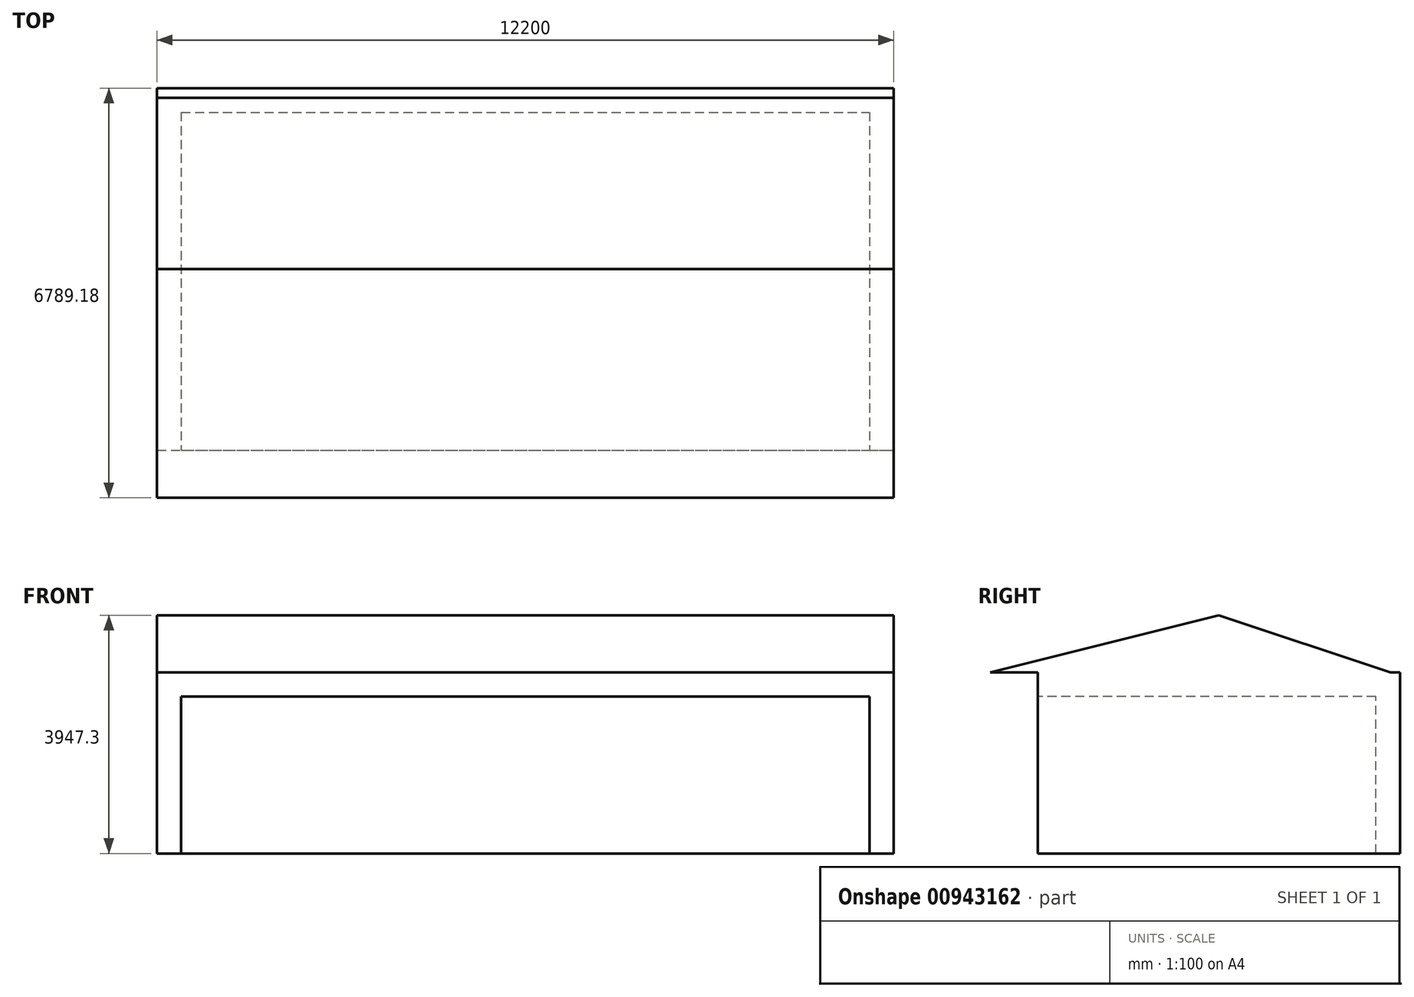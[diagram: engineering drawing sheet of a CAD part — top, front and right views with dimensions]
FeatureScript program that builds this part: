
annotation { "Feature Type Name" : "Feature", "Feature Type Description" : "" }
export const myFeature = defineFeature(function(context is Context, id is Id, definition is map)
    precondition{}
    {
        {
            var Q0;
            Q0=qCreatedBy(makeId("Top.planeOp"),FACE);
            var sketch = newSketch(context, id + "F0", { "sketchPlane" : qUnion([Q0])});
            skLineSegment(sketch, "E0.bottom", {"start": v(0, 0) * mm, "end": v(12200, 0) * mm});
            skLineSegment(sketch, "E0.top", {"start": v(0, -6000) * mm, "end": v(12200, -6000) * mm});
            skLineSegment(sketch, "E0.left", {"start": v(0, 0) * mm, "end": v(0, -6000) * mm});
            skLineSegment(sketch, "E0.right", {"start": v(12200, 0) * mm, "end": v(12200, -6000) * mm});
            skSolve(sketch);
        }
        {
            var Q0;
            Q0 = qSketchRegion(id + "F0", true);
            extrude(context, id + "F1", {"entities" : qUnion([Q0]), "depth" : 3000 * mm, "offsetDistance" : 25 * mm});
        }
        {
            var Q0;
            Q0=makeQuery(id+"F1.opExtrude","SWEPT_FACE",FACE,{"disambiguationData":[OSD([sQuery(id+"F0.wireOp",EDGE,"E0.left")])]});
            var sketch = newSketch(context, id + "F2", { "sketchPlane" : qUnion([Q0])});
            skLineSegment(sketch, "E1", {"start": v(0, 3000) * mm, "end": v(7000, 3000) * mm});
            skLineSegment(sketch, "E2", {"start": v(7000, 3000) * mm, "end": v(3000, 4000) * mm});
            skLineSegment(sketch, "E3", {"start": v(3000, 4000) * mm, "end": v(0, 3000) * mm});
            skSolve(sketch);
        }
        {
            var Q0;
            Q0 = qSketchRegion(id + "F2", true);
            extrude(context, id + "F3", {"entities" : qUnion([Q0]), "operationType" : NewBodyOperationType.ADD, "oppositeDirection" : true, "depth" : 12200 * mm, "offsetDistance" : 25 * mm});
        }
        {
            var Q0;
            Q0=makeQuery(id+"F1.opExtrude","SWEPT_FACE",FACE,{"disambiguationData":[OSD([sQuery(id+"F0.wireOp",EDGE,"E0.top")])]});
            var sketch = newSketch(context, id + "F4", { "sketchPlane" : qUnion([Q0])});
            skLineSegment(sketch, "E4.bottom", {"start": v(400, 0) * mm, "end": v(11800, 0) * mm});
            skLineSegment(sketch, "E4.top", {"start": v(400, 2600) * mm, "end": v(11800, 2600) * mm});
            skLineSegment(sketch, "E4.left", {"start": v(400, 0) * mm, "end": v(400, 2600) * mm});
            skLineSegment(sketch, "E4.right", {"start": v(11800, 0) * mm, "end": v(11800, 2600) * mm});
            skSolve(sketch);
        }
        {
            var Q0;
            Q0 = qSketchRegion(id + "F4", true);
            extrude(context, id + "F5", {"entities" : qUnion([Q0]), "operationType" : NewBodyOperationType.REMOVE, "oppositeDirection" : true, "depth" : 5600 * mm, "offsetDistance" : 25 * mm});
        }
        {
            var Q0;
            Q0=makeQuery(id+"F3.boolean.opBoolean","MERGE",FACE,{"derivedFrom":[makeQuery(id+"F1.opExtrude","SWEPT_FACE",FACE,{"disambiguationData":[OSD([sQuery(id+"F0.wireOp",EDGE,"E0.left")])]}),makeQuery(id+"F3.opExtrude","CAP_FACE",FACE,{"disambiguationData":[OSD([sQuery(id+"F2.wireOp",EDGE,"E1"),sQuery(id+"F2.wireOp",EDGE,"E2"),sQuery(id+"F2.wireOp",EDGE,"E3")])],"isStart":true})]});
            var sketch = newSketch(context, id + "F6", { "sketchPlane" : qUnion([Q0])});
            skLineSegment(sketch, "E5", {"start": v(0, 3000) * mm, "end": v(3000, 4000) * mm});
            skLineSegment(sketch, "E6", {"start": v(3000, 4000) * mm, "end": v(7000, 3000) * mm});
            skLineSegment(sketch, "E7", {"start": v(7000, 3000) * mm, "end": v(6789.18, 3000) * mm});
            skLineSegment(sketch, "E8", {"start": v(6789.18, 3000) * mm, "end": v(3000, 3947.3) * mm});
            skLineSegment(sketch, "E9", {"start": v(3000, 3947.3) * mm, "end": v(158.11, 3000) * mm});
            skLineSegment(sketch, "E10", {"start": v(158.11, 3000) * mm, "end": v(0, 3000) * mm});
            skSolve(sketch);
        }
        {
            var Q0;
            Q0 = qSketchRegion(id + "F6", true);
            extrude(context, id + "F7", {"entities" : qUnion([Q0]), "operationType" : NewBodyOperationType.REMOVE, "oppositeDirection" : true, "depth" : 18300 * mm, "offsetDistance" : 25 * mm});
        }
    });
